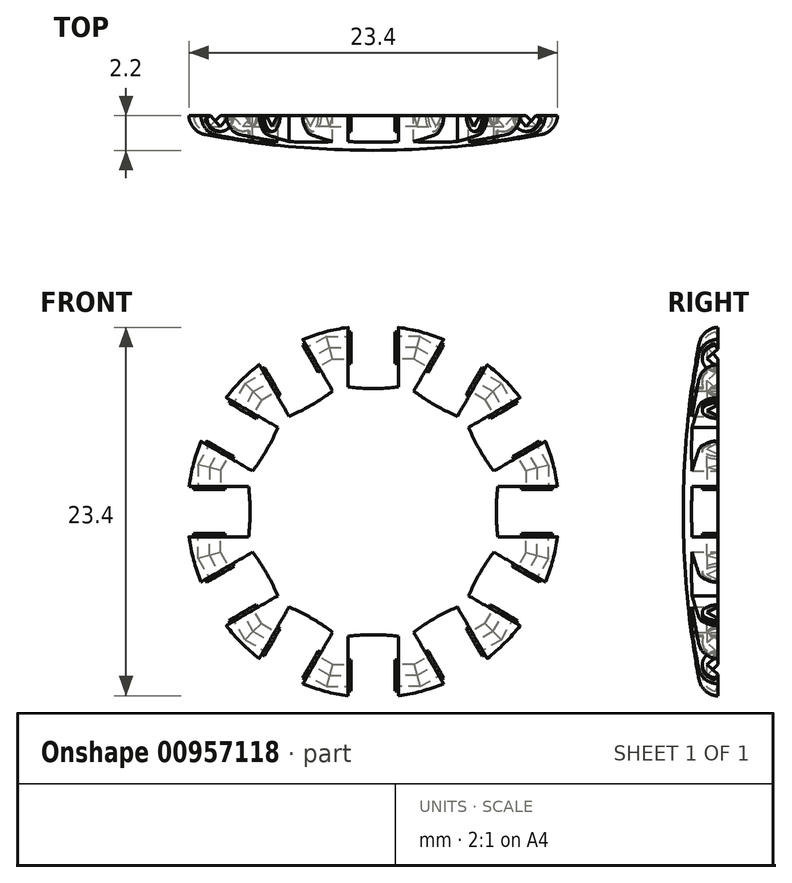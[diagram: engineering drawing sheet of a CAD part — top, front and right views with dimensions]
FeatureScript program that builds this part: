
annotation { "Feature Type Name" : "Feature", "Feature Type Description" : "" }
export const myFeature = defineFeature(function(context is Context, id is Id, definition is map)
    precondition{}
    {
        {
            var Q0;
            Q0=qCreatedBy(makeId("Front.planeOp"),FACE);
            var sketch = newSketch(context, id + "F0", { "sketchPlane" : qUnion([Q0])});
            skCircle(sketch, "E0", {"center": v(0, 0) * mm, "radius": 12.5 * mm, "construction": true});
            skArc(sketch, "E1", {"start": v(1.5, 12.4) * mm, "mid": v(0, 12.5) * mm, "end": v(-1.5, 12.4) * mm});
            skLineSegment(sketch, "E2", {"start": v(-1.5, 12.4) * mm, "end": v(-1.5, 10.9) * mm});
            skLineSegment(sketch, "E3", {"start": v(-1.5, 10.9) * mm, "end": v(-2.5, 10.9) * mm});
            skLineSegment(sketch, "E4", {"start": v(-2.5, 10.9) * mm, "end": v(-2.5, 10.4) * mm});
            skLineSegment(sketch, "E5", {"start": v(0, 0) * mm, "end": v(0, 14.4) * mm, "construction": true});
            skLineSegment(sketch, "E6.MirrorCS", {"start": v(1.5, 10.9) * mm, "end": v(2.5, 10.9) * mm});
            skLineSegment(sketch, "E7.MirrorCS", {"start": v(2.5, 10.9) * mm, "end": v(2.5, 10.4) * mm});
            skLineSegment(sketch, "E8.MirrorCS", {"start": v(1.5, 12.4) * mm, "end": v(1.5, 10.9) * mm});
            skLineSegment(sketch, "E9", {"start": v(-3.4, 10.4) * mm, "end": v(4.36, 10.4) * mm, "construction": true});
            skLineSegment(sketch, "E10.MirrorCS", {"start": v(2.5, 9.9) * mm, "end": v(2.5, 10.4) * mm});
            skLineSegment(sketch, "E11.MirrorCS", {"start": v(1.5, 9.9) * mm, "end": v(2.5, 9.9) * mm});
            skLineSegment(sketch, "E12.MirrorCS", {"start": v(-1.5, 9.9) * mm, "end": v(-2.5, 9.9) * mm});
            skLineSegment(sketch, "E13.MirrorCS", {"start": v(-1.5, 8.4) * mm, "end": v(-1.5, 9.9) * mm});
            skArc(sketch, "E14.MirrorCS", {"start": v(1.5, 8.4) * mm, "mid": v(0, 8.32) * mm, "end": v(-1.5, 8.4) * mm});
            skLineSegment(sketch, "E15.MirrorCS", {"start": v(-2.5, 9.9) * mm, "end": v(-2.5, 10.4) * mm});
            skLineSegment(sketch, "E16.MirrorCS", {"start": v(1.5, 8.4) * mm, "end": v(1.5, 9.9) * mm});
            skLineSegment(sketch, "E17.1.0", {"start": v(-5.5, 6.53) * mm, "end": v(-6.25, 7.83) * mm});
            skLineSegment(sketch, "E17.1.1", {"start": v(-3.66, 9.33) * mm, "end": v(-2.79, 9.83) * mm});
            skLineSegment(sketch, "E17.1.2", {"start": v(-7.5, 10) * mm, "end": v(-6.75, 8.7) * mm});
            skLineSegment(sketch, "E17.1.3", {"start": v(-4.9, 11.5) * mm, "end": v(-4.16, 10.2) * mm});
            skLineSegment(sketch, "E17.1.4", {"start": v(-6.75, 8.7) * mm, "end": v(-7.62, 8.2) * mm});
            skLineSegment(sketch, "E17.1.5", {"start": v(-4.16, 10.2) * mm, "end": v(-3.29, 10.7) * mm});
            skArc(sketch, "E17.1.6", {"start": v(-4.9, 11.5) * mm, "mid": v(-6.25, 10.83) * mm, "end": v(-7.5, 10) * mm});
            skLineSegment(sketch, "E17.1.7", {"start": v(-2.9, 8.03) * mm, "end": v(-3.66, 9.33) * mm});
            skLineSegment(sketch, "E17.1.8", {"start": v(-6.25, 7.83) * mm, "end": v(-7.12, 7.33) * mm});
            skLineSegment(sketch, "E17.1.9", {"start": v(-8.14, 7.32) * mm, "end": v(-1.43, 11.2) * mm, "construction": true});
            skArc(sketch, "E17.1.10", {"start": v(-2.9, 8.03) * mm, "mid": v(-4.16, 7.2) * mm, "end": v(-5.5, 6.53) * mm});
            skLineSegment(sketch, "E17.1.11", {"start": v(-7.62, 8.2) * mm, "end": v(-7.37, 7.77) * mm});
            skLineSegment(sketch, "E17.1.12", {"start": v(-2.79, 9.83) * mm, "end": v(-3.04, 10.27) * mm});
            skLineSegment(sketch, "E17.1.13", {"start": v(-3.29, 10.7) * mm, "end": v(-3.04, 10.27) * mm});
            skLineSegment(sketch, "E17.1.14", {"start": v(-7.12, 7.33) * mm, "end": v(-7.37, 7.77) * mm});
            skLineSegment(sketch, "E17.2.0", {"start": v(-8.03, 2.9) * mm, "end": v(-9.33, 3.66) * mm});
            skLineSegment(sketch, "E17.2.1", {"start": v(-7.83, 6.25) * mm, "end": v(-7.33, 7.12) * mm});
            skLineSegment(sketch, "E17.2.2", {"start": v(-11.5, 4.9) * mm, "end": v(-10.2, 4.16) * mm});
            skLineSegment(sketch, "E17.2.3", {"start": v(-10, 7.5) * mm, "end": v(-8.7, 6.75) * mm});
            skLineSegment(sketch, "E17.2.4", {"start": v(-10.2, 4.16) * mm, "end": v(-10.7, 3.29) * mm});
            skLineSegment(sketch, "E17.2.5", {"start": v(-8.7, 6.75) * mm, "end": v(-8.2, 7.62) * mm});
            skArc(sketch, "E17.2.6", {"start": v(-10, 7.5) * mm, "mid": v(-10.83, 6.25) * mm, "end": v(-11.5, 4.9) * mm});
            skLineSegment(sketch, "E17.2.7", {"start": v(-6.53, 5.5) * mm, "end": v(-7.83, 6.25) * mm});
            skLineSegment(sketch, "E17.2.8", {"start": v(-9.33, 3.66) * mm, "end": v(-9.83, 2.79) * mm});
            skLineSegment(sketch, "E17.2.9", {"start": v(-10.71, 2.26) * mm, "end": v(-6.83, 8.98) * mm, "construction": true});
            skArc(sketch, "E17.2.10", {"start": v(-6.53, 5.5) * mm, "mid": v(-7.2, 4.16) * mm, "end": v(-8.03, 2.9) * mm});
            skLineSegment(sketch, "E17.2.11", {"start": v(-10.7, 3.29) * mm, "end": v(-10.27, 3.04) * mm});
            skLineSegment(sketch, "E17.2.12", {"start": v(-7.33, 7.12) * mm, "end": v(-7.77, 7.37) * mm});
            skLineSegment(sketch, "E17.2.13", {"start": v(-8.2, 7.62) * mm, "end": v(-7.77, 7.37) * mm});
            skLineSegment(sketch, "E17.2.14", {"start": v(-9.83, 2.79) * mm, "end": v(-10.27, 3.04) * mm});
            skLineSegment(sketch, "E17.3.0", {"start": v(-8.4, -1.5) * mm, "end": v(-9.9, -1.5) * mm});
            skLineSegment(sketch, "E17.3.1", {"start": v(-9.9, 1.5) * mm, "end": v(-9.9, 2.5) * mm});
            skLineSegment(sketch, "E17.3.2", {"start": v(-12.4, -1.5) * mm, "end": v(-10.9, -1.5) * mm});
            skLineSegment(sketch, "E17.3.3", {"start": v(-12.4, 1.5) * mm, "end": v(-10.9, 1.5) * mm});
            skLineSegment(sketch, "E17.3.4", {"start": v(-10.9, -1.5) * mm, "end": v(-10.9, -2.5) * mm});
            skLineSegment(sketch, "E17.3.5", {"start": v(-10.9, 1.5) * mm, "end": v(-10.9, 2.5) * mm});
            skArc(sketch, "E17.3.6", {"start": v(-12.4, 1.5) * mm, "mid": v(-12.5, 0) * mm, "end": v(-12.4, -1.5) * mm});
            skLineSegment(sketch, "E17.3.7", {"start": v(-8.4, 1.5) * mm, "end": v(-9.9, 1.5) * mm});
            skLineSegment(sketch, "E17.3.8", {"start": v(-9.9, -1.5) * mm, "end": v(-9.9, -2.5) * mm});
            skLineSegment(sketch, "E17.3.9", {"start": v(-10.4, -3.4) * mm, "end": v(-10.4, 4.36) * mm, "construction": true});
            skArc(sketch, "E17.3.10", {"start": v(-8.4, 1.5) * mm, "mid": v(-8.32, 0) * mm, "end": v(-8.4, -1.5) * mm});
            skLineSegment(sketch, "E17.3.11", {"start": v(-10.9, -2.5) * mm, "end": v(-10.4, -2.5) * mm});
            skLineSegment(sketch, "E17.3.12", {"start": v(-9.9, 2.5) * mm, "end": v(-10.4, 2.5) * mm});
            skLineSegment(sketch, "E17.3.13", {"start": v(-10.9, 2.5) * mm, "end": v(-10.4, 2.5) * mm});
            skLineSegment(sketch, "E17.3.14", {"start": v(-9.9, -2.5) * mm, "end": v(-10.4, -2.5) * mm});
            skLineSegment(sketch, "E17.4.0", {"start": v(-6.53, -5.5) * mm, "end": v(-7.83, -6.25) * mm});
            skLineSegment(sketch, "E17.4.1", {"start": v(-9.33, -3.66) * mm, "end": v(-9.83, -2.79) * mm});
            skLineSegment(sketch, "E17.4.2", {"start": v(-10, -7.5) * mm, "end": v(-8.7, -6.75) * mm});
            skLineSegment(sketch, "E17.4.3", {"start": v(-11.5, -4.9) * mm, "end": v(-10.2, -4.16) * mm});
            skLineSegment(sketch, "E17.4.4", {"start": v(-8.7, -6.75) * mm, "end": v(-8.2, -7.62) * mm});
            skLineSegment(sketch, "E17.4.5", {"start": v(-10.2, -4.16) * mm, "end": v(-10.7, -3.29) * mm});
            skArc(sketch, "E17.4.6", {"start": v(-11.5, -4.9) * mm, "mid": v(-10.83, -6.25) * mm, "end": v(-10, -7.5) * mm});
            skLineSegment(sketch, "E17.4.7", {"start": v(-8.03, -2.9) * mm, "end": v(-9.33, -3.66) * mm});
            skLineSegment(sketch, "E17.4.8", {"start": v(-7.83, -6.25) * mm, "end": v(-7.33, -7.12) * mm});
            skLineSegment(sketch, "E17.4.9", {"start": v(-7.32, -8.14) * mm, "end": v(-11.2, -1.43) * mm, "construction": true});
            skArc(sketch, "E17.4.10", {"start": v(-8.03, -2.9) * mm, "mid": v(-7.2, -4.16) * mm, "end": v(-6.53, -5.5) * mm});
            skLineSegment(sketch, "E17.4.11", {"start": v(-8.2, -7.62) * mm, "end": v(-7.77, -7.37) * mm});
            skLineSegment(sketch, "E17.4.12", {"start": v(-9.83, -2.79) * mm, "end": v(-10.27, -3.04) * mm});
            skLineSegment(sketch, "E17.4.13", {"start": v(-10.7, -3.29) * mm, "end": v(-10.27, -3.04) * mm});
            skLineSegment(sketch, "E17.4.14", {"start": v(-7.33, -7.12) * mm, "end": v(-7.77, -7.37) * mm});
            skLineSegment(sketch, "E17.5.0", {"start": v(-2.9, -8.03) * mm, "end": v(-3.66, -9.33) * mm});
            skLineSegment(sketch, "E17.5.1", {"start": v(-6.25, -7.83) * mm, "end": v(-7.12, -7.33) * mm});
            skLineSegment(sketch, "E17.5.2", {"start": v(-4.9, -11.5) * mm, "end": v(-4.16, -10.2) * mm});
            skLineSegment(sketch, "E17.5.3", {"start": v(-7.5, -10) * mm, "end": v(-6.75, -8.7) * mm});
            skLineSegment(sketch, "E17.5.4", {"start": v(-4.16, -10.2) * mm, "end": v(-3.29, -10.7) * mm});
            skLineSegment(sketch, "E17.5.5", {"start": v(-6.75, -8.7) * mm, "end": v(-7.62, -8.2) * mm});
            skArc(sketch, "E17.5.6", {"start": v(-7.5, -10) * mm, "mid": v(-6.25, -10.83) * mm, "end": v(-4.9, -11.5) * mm});
            skLineSegment(sketch, "E17.5.7", {"start": v(-5.5, -6.53) * mm, "end": v(-6.25, -7.83) * mm});
            skLineSegment(sketch, "E17.5.8", {"start": v(-3.66, -9.33) * mm, "end": v(-2.79, -9.83) * mm});
            skLineSegment(sketch, "E17.5.9", {"start": v(-2.26, -10.71) * mm, "end": v(-8.98, -6.83) * mm, "construction": true});
            skArc(sketch, "E17.5.10", {"start": v(-5.5, -6.53) * mm, "mid": v(-4.16, -7.2) * mm, "end": v(-2.9, -8.03) * mm});
            skLineSegment(sketch, "E17.5.11", {"start": v(-3.29, -10.7) * mm, "end": v(-3.04, -10.27) * mm});
            skLineSegment(sketch, "E17.5.12", {"start": v(-7.12, -7.33) * mm, "end": v(-7.37, -7.77) * mm});
            skLineSegment(sketch, "E17.5.13", {"start": v(-7.62, -8.2) * mm, "end": v(-7.37, -7.77) * mm});
            skLineSegment(sketch, "E17.5.14", {"start": v(-2.79, -9.83) * mm, "end": v(-3.04, -10.27) * mm});
            skLineSegment(sketch, "E17.6.0", {"start": v(1.5, -8.4) * mm, "end": v(1.5, -9.9) * mm});
            skLineSegment(sketch, "E17.6.1", {"start": v(-1.5, -9.9) * mm, "end": v(-2.5, -9.9) * mm});
            skLineSegment(sketch, "E17.6.2", {"start": v(1.5, -12.4) * mm, "end": v(1.5, -10.9) * mm});
            skLineSegment(sketch, "E17.6.3", {"start": v(-1.5, -12.4) * mm, "end": v(-1.5, -10.9) * mm});
            skLineSegment(sketch, "E17.6.4", {"start": v(1.5, -10.9) * mm, "end": v(2.5, -10.9) * mm});
            skLineSegment(sketch, "E17.6.5", {"start": v(-1.5, -10.9) * mm, "end": v(-2.5, -10.9) * mm});
            skArc(sketch, "E17.6.6", {"start": v(-1.5, -12.4) * mm, "mid": v(0, -12.5) * mm, "end": v(1.5, -12.4) * mm});
            skLineSegment(sketch, "E17.6.7", {"start": v(-1.5, -8.4) * mm, "end": v(-1.5, -9.9) * mm});
            skLineSegment(sketch, "E17.6.8", {"start": v(1.5, -9.9) * mm, "end": v(2.5, -9.9) * mm});
            skLineSegment(sketch, "E17.6.9", {"start": v(3.4, -10.4) * mm, "end": v(-4.36, -10.4) * mm, "construction": true});
            skArc(sketch, "E17.6.10", {"start": v(-1.5, -8.4) * mm, "mid": v(0, -8.32) * mm, "end": v(1.5, -8.4) * mm});
            skLineSegment(sketch, "E17.6.11", {"start": v(2.5, -10.9) * mm, "end": v(2.5, -10.4) * mm});
            skLineSegment(sketch, "E17.6.12", {"start": v(-2.5, -9.9) * mm, "end": v(-2.5, -10.4) * mm});
            skLineSegment(sketch, "E17.6.13", {"start": v(-2.5, -10.9) * mm, "end": v(-2.5, -10.4) * mm});
            skLineSegment(sketch, "E17.6.14", {"start": v(2.5, -9.9) * mm, "end": v(2.5, -10.4) * mm});
            skLineSegment(sketch, "E17.7.0", {"start": v(5.5, -6.53) * mm, "end": v(6.25, -7.83) * mm});
            skLineSegment(sketch, "E17.7.1", {"start": v(3.66, -9.33) * mm, "end": v(2.79, -9.83) * mm});
            skLineSegment(sketch, "E17.7.2", {"start": v(7.5, -10) * mm, "end": v(6.75, -8.7) * mm});
            skLineSegment(sketch, "E17.7.3", {"start": v(4.9, -11.5) * mm, "end": v(4.16, -10.2) * mm});
            skLineSegment(sketch, "E17.7.4", {"start": v(6.75, -8.7) * mm, "end": v(7.62, -8.2) * mm});
            skLineSegment(sketch, "E17.7.5", {"start": v(4.16, -10.2) * mm, "end": v(3.29, -10.7) * mm});
            skArc(sketch, "E17.7.6", {"start": v(4.9, -11.5) * mm, "mid": v(6.25, -10.83) * mm, "end": v(7.5, -10) * mm});
            skLineSegment(sketch, "E17.7.7", {"start": v(2.9, -8.03) * mm, "end": v(3.66, -9.33) * mm});
            skLineSegment(sketch, "E17.7.8", {"start": v(6.25, -7.83) * mm, "end": v(7.12, -7.33) * mm});
            skLineSegment(sketch, "E17.7.9", {"start": v(8.14, -7.32) * mm, "end": v(1.43, -11.2) * mm, "construction": true});
            skArc(sketch, "E17.7.10", {"start": v(2.9, -8.03) * mm, "mid": v(4.16, -7.2) * mm, "end": v(5.5, -6.53) * mm});
            skLineSegment(sketch, "E17.7.11", {"start": v(7.62, -8.2) * mm, "end": v(7.37, -7.77) * mm});
            skLineSegment(sketch, "E17.7.12", {"start": v(2.79, -9.83) * mm, "end": v(3.04, -10.27) * mm});
            skLineSegment(sketch, "E17.7.13", {"start": v(3.29, -10.7) * mm, "end": v(3.04, -10.27) * mm});
            skLineSegment(sketch, "E17.7.14", {"start": v(7.12, -7.33) * mm, "end": v(7.37, -7.77) * mm});
            skLineSegment(sketch, "E17.8.0", {"start": v(8.03, -2.9) * mm, "end": v(9.33, -3.66) * mm});
            skLineSegment(sketch, "E17.8.1", {"start": v(7.83, -6.25) * mm, "end": v(7.33, -7.12) * mm});
            skLineSegment(sketch, "E17.8.2", {"start": v(11.5, -4.9) * mm, "end": v(10.2, -4.16) * mm});
            skLineSegment(sketch, "E17.8.3", {"start": v(10, -7.5) * mm, "end": v(8.7, -6.75) * mm});
            skLineSegment(sketch, "E17.8.4", {"start": v(10.2, -4.16) * mm, "end": v(10.7, -3.29) * mm});
            skLineSegment(sketch, "E17.8.5", {"start": v(8.7, -6.75) * mm, "end": v(8.2, -7.62) * mm});
            skArc(sketch, "E17.8.6", {"start": v(10, -7.5) * mm, "mid": v(10.83, -6.25) * mm, "end": v(11.5, -4.9) * mm});
            skLineSegment(sketch, "E17.8.7", {"start": v(6.53, -5.5) * mm, "end": v(7.83, -6.25) * mm});
            skLineSegment(sketch, "E17.8.8", {"start": v(9.33, -3.66) * mm, "end": v(9.83, -2.79) * mm});
            skLineSegment(sketch, "E17.8.9", {"start": v(10.71, -2.26) * mm, "end": v(6.83, -8.98) * mm, "construction": true});
            skArc(sketch, "E17.8.10", {"start": v(6.53, -5.5) * mm, "mid": v(7.2, -4.16) * mm, "end": v(8.03, -2.9) * mm});
            skLineSegment(sketch, "E17.8.11", {"start": v(10.7, -3.29) * mm, "end": v(10.27, -3.04) * mm});
            skLineSegment(sketch, "E17.8.12", {"start": v(7.33, -7.12) * mm, "end": v(7.77, -7.37) * mm});
            skLineSegment(sketch, "E17.8.13", {"start": v(8.2, -7.62) * mm, "end": v(7.77, -7.37) * mm});
            skLineSegment(sketch, "E17.8.14", {"start": v(9.83, -2.79) * mm, "end": v(10.27, -3.04) * mm});
            skLineSegment(sketch, "E17.9.0", {"start": v(8.4, 1.5) * mm, "end": v(9.9, 1.5) * mm});
            skLineSegment(sketch, "E17.9.1", {"start": v(9.9, -1.5) * mm, "end": v(9.9, -2.5) * mm});
            skLineSegment(sketch, "E17.9.2", {"start": v(12.4, 1.5) * mm, "end": v(10.9, 1.5) * mm});
            skLineSegment(sketch, "E17.9.3", {"start": v(12.4, -1.5) * mm, "end": v(10.9, -1.5) * mm});
            skLineSegment(sketch, "E17.9.4", {"start": v(10.9, 1.5) * mm, "end": v(10.9, 2.5) * mm});
            skLineSegment(sketch, "E17.9.5", {"start": v(10.9, -1.5) * mm, "end": v(10.9, -2.5) * mm});
            skArc(sketch, "E17.9.6", {"start": v(12.4, -1.5) * mm, "mid": v(12.5, 0) * mm, "end": v(12.4, 1.5) * mm});
            skLineSegment(sketch, "E17.9.7", {"start": v(8.4, -1.5) * mm, "end": v(9.9, -1.5) * mm});
            skLineSegment(sketch, "E17.9.8", {"start": v(9.9, 1.5) * mm, "end": v(9.9, 2.5) * mm});
            skLineSegment(sketch, "E17.9.9", {"start": v(10.4, 3.4) * mm, "end": v(10.4, -4.36) * mm, "construction": true});
            skArc(sketch, "E17.9.10", {"start": v(8.4, -1.5) * mm, "mid": v(8.32, 0) * mm, "end": v(8.4, 1.5) * mm});
            skLineSegment(sketch, "E17.9.11", {"start": v(10.9, 2.5) * mm, "end": v(10.4, 2.5) * mm});
            skLineSegment(sketch, "E17.9.12", {"start": v(9.9, -2.5) * mm, "end": v(10.4, -2.5) * mm});
            skLineSegment(sketch, "E17.9.13", {"start": v(10.9, -2.5) * mm, "end": v(10.4, -2.5) * mm});
            skLineSegment(sketch, "E17.9.14", {"start": v(9.9, 2.5) * mm, "end": v(10.4, 2.5) * mm});
            skLineSegment(sketch, "E18.1.10.0", {"start": v(6.53, 5.5) * mm, "end": v(7.83, 6.25) * mm});
            skLineSegment(sketch, "E18.3.10.0", {"start": v(9.33, 3.66) * mm, "end": v(9.83, 2.79) * mm});
            skLineSegment(sketch, "E18.6.10.0", {"start": v(10, 7.5) * mm, "end": v(8.7, 6.75) * mm});
            skLineSegment(sketch, "E18.9.10.0", {"start": v(11.5, 4.9) * mm, "end": v(10.2, 4.16) * mm});
            skLineSegment(sketch, "E18.12.10.0", {"start": v(8.7, 6.75) * mm, "end": v(8.2, 7.62) * mm});
            skLineSegment(sketch, "E18.15.10.0", {"start": v(10.2, 4.16) * mm, "end": v(10.7, 3.29) * mm});
            skArc(sketch, "E18.18.10.0", {"start": v(11.5, 4.9) * mm, "mid": v(10.83, 6.25) * mm, "end": v(10, 7.5) * mm});
            skLineSegment(sketch, "E18.22.10.0", {"start": v(8.03, 2.9) * mm, "end": v(9.33, 3.66) * mm});
            skLineSegment(sketch, "E18.25.10.0", {"start": v(7.83, 6.25) * mm, "end": v(7.33, 7.12) * mm});
            skLineSegment(sketch, "E18.28.10.0", {"start": v(7.32, 8.14) * mm, "end": v(11.2, 1.43) * mm, "construction": true});
            skArc(sketch, "E18.31.10.0", {"start": v(8.03, 2.9) * mm, "mid": v(7.2, 4.16) * mm, "end": v(6.53, 5.5) * mm});
            skLineSegment(sketch, "E18.35.10.0", {"start": v(8.2, 7.62) * mm, "end": v(7.77, 7.37) * mm});
            skLineSegment(sketch, "E18.38.10.0", {"start": v(9.83, 2.79) * mm, "end": v(10.27, 3.04) * mm});
            skLineSegment(sketch, "E18.41.10.0", {"start": v(10.7, 3.29) * mm, "end": v(10.27, 3.04) * mm});
            skLineSegment(sketch, "E18.44.10.0", {"start": v(7.33, 7.12) * mm, "end": v(7.77, 7.37) * mm});
            skLineSegment(sketch, "E18.1.11.0", {"start": v(2.9, 8.03) * mm, "end": v(3.66, 9.33) * mm});
            skLineSegment(sketch, "E18.3.11.0", {"start": v(6.25, 7.83) * mm, "end": v(7.12, 7.33) * mm});
            skLineSegment(sketch, "E18.6.11.0", {"start": v(4.9, 11.5) * mm, "end": v(4.16, 10.2) * mm});
            skLineSegment(sketch, "E18.9.11.0", {"start": v(7.5, 10) * mm, "end": v(6.75, 8.7) * mm});
            skLineSegment(sketch, "E18.12.11.0", {"start": v(4.16, 10.2) * mm, "end": v(3.29, 10.7) * mm});
            skLineSegment(sketch, "E18.15.11.0", {"start": v(6.75, 8.7) * mm, "end": v(7.62, 8.2) * mm});
            skArc(sketch, "E18.18.11.0", {"start": v(7.5, 10) * mm, "mid": v(6.25, 10.83) * mm, "end": v(4.9, 11.5) * mm});
            skLineSegment(sketch, "E18.22.11.0", {"start": v(5.5, 6.53) * mm, "end": v(6.25, 7.83) * mm});
            skLineSegment(sketch, "E18.25.11.0", {"start": v(3.66, 9.33) * mm, "end": v(2.79, 9.83) * mm});
            skLineSegment(sketch, "E18.28.11.0", {"start": v(2.26, 10.71) * mm, "end": v(8.98, 6.83) * mm, "construction": true});
            skArc(sketch, "E18.31.11.0", {"start": v(5.5, 6.53) * mm, "mid": v(4.16, 7.2) * mm, "end": v(2.9, 8.03) * mm});
            skLineSegment(sketch, "E18.35.11.0", {"start": v(3.29, 10.7) * mm, "end": v(3.04, 10.27) * mm});
            skLineSegment(sketch, "E18.38.11.0", {"start": v(7.12, 7.33) * mm, "end": v(7.37, 7.77) * mm});
            skLineSegment(sketch, "E18.41.11.0", {"start": v(7.62, 8.2) * mm, "end": v(7.37, 7.77) * mm});
            skLineSegment(sketch, "E18.44.11.0", {"start": v(2.79, 9.83) * mm, "end": v(3.04, 10.27) * mm});
            skLineSegment(sketch, "E19", {"start": v(-4.9, 11.5) * mm, "end": v(-1.5, 12.4) * mm, "construction": true});
            skLineSegment(sketch, "E20", {"start": v(-4.92, 11.62) * mm, "end": v(-1.74, 12.48) * mm, "construction": true});
            skSolve(sketch);
        }
        {
            var Q0;
            Q0=qCreatedBy(makeId("Front.planeOp"),FACE);
            var sketch = newSketch(context, id + "F1", { "sketchPlane" : qUnion([Q0])});
            skLineSegment(sketch, "E21", {"start": v(0, 0) * mm, "end": v(0, 16.74) * mm, "construction": true});
            skLineSegment(sketch, "E22", {"start": v(0, 0) * mm, "end": v(3.06, 11.4) * mm, "construction": true});
            skArc(sketch, "E23", {"start": v(0, 7.82) * mm, "mid": v(0.8, 7.84) * mm, "end": v(1.6, 7.92) * mm});
            skLineSegment(sketch, "E24", {"start": v(1.6, 7.92) * mm, "end": v(1.6, 11.4) * mm});
            skLineSegment(sketch, "E25", {"start": v(0, 7.82) * mm, "end": v(0, 0) * mm});
            skLineSegment(sketch, "E26", {"start": v(3.06, 11.4) * mm, "end": v(0, 0) * mm});
            skLineSegment(sketch, "E27", {"start": v(1.6, 11.4) * mm, "end": v(3.06, 11.4) * mm, "construction": true});
            skLineSegment(sketch, "E28.trimOffspring", {"start": v(3.1, 11.6) * mm, "end": v(4.38, 16.35) * mm, "construction": true});
            skLineSegment(sketch, "E29", {"start": v(3.06, 11.4) * mm, "end": v(1.6, 11.8) * mm});
            skLineSegment(sketch, "E30", {"start": v(1.6, 11.8) * mm, "end": v(1.6, 11.4) * mm});
            skSolve(sketch);
        }
        {
            var Q0;
            Q0 = qSketchRegion(id + "F1", true);
            extrude(context, id + "F2", {"entities" : qUnion([Q0]), "depth" : 2.2 * mm, "offsetDistance" : 25 * mm});
        }
        {
            var Q0;
            Q0=makeQuery(id+"F2.opExtrude","SWEPT_FACE",FACE,{"disambiguationData":[OSD([sQuery(id+"F1.wireOp",EDGE,"E24")])]});
            var sketch = newSketch(context, id + "F3", { "sketchPlane" : qUnion([Q0])});
            skCircle(sketch, "E31", {"center": v(0, 10.4) * mm, "radius": 0.5 * mm, "construction": true});
            skLineSegment(sketch, "E32", {"start": v(0, 11.12) * mm, "end": v(0.7, 10.4) * mm});
            skLineSegment(sketch, "E33", {"start": v(0.7, 10.4) * mm, "end": v(0, 9.7) * mm});
            skLineSegment(sketch, "E34", {"start": v(0, 11.12) * mm, "end": v(0, 9.7) * mm});
            skSolve(sketch);
        }
        {
            var Q0;
            Q0=makeQuery(id+"F3.imprint","IMPRINT",FACE,{"disambiguationData":[TD([[makeQuery(id+"F3.imprint","IMPRINT",EDGE,{"derivedFrom":sQuery(id+"F3.wireOp",EDGE,"E32")}),-1.0]])]});
            extrude(context, id + "F4", {"entities" : qUnion([Q0]), "operationType" : NewBodyOperationType.REMOVE, "endBound" : BoundingType.THROUGH_ALL, "oppositeDirection" : true, "depth" : 25 * mm, "offsetDistance" : 25 * mm});
        }
        {
            var Q0;
            Q0=makeQuery(id+"F2.opExtrude","SWEPT_FACE",FACE,{"disambiguationData":[OSD([sQuery(id+"F1.wireOp",EDGE,"E26")])]});
            var sketch = newSketch(context, id + "F5", { "sketchPlane" : qUnion([Q0])});
            skArc(sketch, "E35", {"start": v(-1.2, 10.78) * mm, "mid": v(-1.95, 5.41) * mm, "end": v(-2.2, 0) * mm});
            skLineSegment(sketch, "E36", {"start": v(1.37, 10.78) * mm, "end": v(-3.78, 10.78) * mm, "construction": true});
            skPoint(sketch, "E37", {"position": v(-1.2, 10.78) * mm});
            skLineSegment(sketch, "E38", {"start": v(0, 0) * mm, "end": v(-2.2, 0) * mm});
            skLineSegment(sketch, "E39", {"start": v(-2.2, 0) * mm, "end": v(-2.2, 0) * mm});
            skLineSegment(sketch, "E40", {"start": v(0, 11.5) * mm, "end": v(0, 10.04) * mm, "construction": true});
            skPoint(sketch, "E41", {"position": v(0, 10.78) * mm});
            skArc(sketch, "E42", {"start": v(0, 11.81) * mm, "mid": v(-0.1, 11.8) * mm, "end": v(-0.19, 11.8) * mm});
            skArc(sketch, "E43", {"start": v(-0.19, 11.8) * mm, "mid": v(-0.86, 11.44) * mm, "end": v(-1.2, 10.78) * mm});
            skPoint(sketch, "E44", {"position": v(-0.7, 10.78) * mm});
            skLineSegment(sketch, "E45", {"start": v(-2.2, 11.81) * mm, "end": v(-2.2, 0) * mm});
            skLineSegment(sketch, "E46", {"start": v(0, 11.81) * mm, "end": v(0, 12.97) * mm});
            skLineSegment(sketch, "E47", {"start": v(0, 12.97) * mm, "end": v(-2.2, 12.97) * mm});
            skLineSegment(sketch, "E48", {"start": v(-2.2, 12.97) * mm, "end": v(-2.2, 11.81) * mm});
            skSolve(sketch);
        }
        {
            var Q0;
            Q0 = qSketchRegion(id + "F5", true);
            var Q1;
            Q1=makeQuery(id+"F2.opExtrude","SWEPT_EDGE",EDGE,{"disambiguationData":[OSD([sQuery(id+"F1.wireOp",EDGE,"E25"),sQuery(id+"F1.wireOp",EDGE,"E26")])]});
            revolve(context, id + "F6", {"operationType" : NewBodyOperationType.REMOVE, "surfaceOperationType" : NewSurfaceOperationType.NEW, "entities" : qUnion([Q0]), "axis" : qUnion([Q1]), "revolveType" : RevolveType.ONE_DIRECTION, "oppositeDirection" : true, "angle" : 30 * degree});
        }
        {
            var Q0;
            Q0=makeQuery(id+"F2.opExtrude","SWEPT_FACE",FACE,{"disambiguationData":[OSD([sQuery(id+"F1.wireOp",EDGE,"E24")])]});
            var sketch = newSketch(context, id + "F7", { "sketchPlane" : qUnion([Q0])});
            skArc(sketch, "E49", {"start": v(0, 9.4) * mm, "mid": v(1, 10.33) * mm, "end": v(0.17, 11.4) * mm});
            skLineSegment(sketch, "E50", {"start": v(0.17, 11.4) * mm, "end": v(0, 11.12) * mm});
            skLineSegment(sketch, "E51", {"start": v(0, 11.12) * mm, "end": v(0.7, 10.4) * mm});
            skLineSegment(sketch, "E52", {"start": v(0.7, 10.4) * mm, "end": v(0, 9.7) * mm});
            skLineSegment(sketch, "E53", {"start": v(0, 9.7) * mm, "end": v(0, 9.4) * mm});
            skSolve(sketch);
        }
        {
            var Q0;
            Q0 = qSketchRegion(id + "F7", true);
            extrude(context, id + "F8", {"entities" : qUnion([Q0]), "operationType" : NewBodyOperationType.ADD, "depth" : 0.2 * mm, "offsetDistance" : 25 * mm});
        }
        {
            var Q0;
            Q0=makeQuery(id+"F2.opExtrude","SWEPT_BODY",BODY,{"disambiguationData":[OSD([sQuery(id+"F1.wireOp",EDGE,"E23"),sQuery(id+"F1.wireOp",EDGE,"E24"),sQuery(id+"F1.wireOp",EDGE,"12pXdVJX-N50U-wwqA-nHGD-GnBIGzNj4h2q"),sQuery(id+"F1.wireOp",EDGE,"E25"),sQuery(id+"F1.wireOp",EDGE,"E26")])]});
            var Q1;
            Q1=makeQuery(id+"F2.opExtrude","SWEPT_FACE",FACE,{"disambiguationData":[OSD([sQuery(id+"F1.wireOp",EDGE,"E26")])]});
            mirror(context, id + "F9", {"operationType" : NewBodyOperationType.ADD, "entities" : qUnion([Q0]), "mirrorPlane" : qUnion([Q1])});
        }
        {
            var Q0;
            Q0=makeQuery(id+"F2.opExtrude","SWEPT_BODY",BODY,{"disambiguationData":[OSD([sQuery(id+"F1.wireOp",EDGE,"E23"),sQuery(id+"F1.wireOp",EDGE,"E24"),sQuery(id+"F1.wireOp",EDGE,"12pXdVJX-N50U-wwqA-nHGD-GnBIGzNj4h2q"),sQuery(id+"F1.wireOp",EDGE,"E25"),sQuery(id+"F1.wireOp",EDGE,"E26")])]});
            var Q1;
            {var subQ0=makeQuery(id+"F2.opExtrude","SWEPT_EDGE",EDGE,{"disambiguationData":[OSD([sQuery(id+"F1.wireOp",EDGE,"E25"),sQuery(id+"F1.wireOp",EDGE,"E26")])]});Q1=makeQuery(id+"F9.boolean.opBoolean","MERGE",EDGE,{"derivedFrom":[subQ0,makeQuery(id+"F9.opPattern","COPY",EDGE,{"derivedFrom":subQ0,"instanceName":"1"})]});}
            circularPattern(context, id + "F10", {"operationType" : NewBodyOperationType.ADD, "entities" : qUnion([Q0]), "axis" : qUnion([Q1]), "angle" : 360 * degree, "instanceCount" : 12, "equalSpace" : true});
        }
    });
